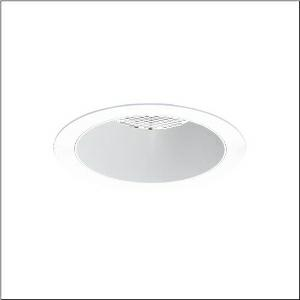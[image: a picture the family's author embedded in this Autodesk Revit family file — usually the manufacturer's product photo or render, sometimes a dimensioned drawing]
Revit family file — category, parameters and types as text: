
# Revit family: lunis_21_xl_51db18ef91c
name_source: partatom
category: Lighting Fixtures
units: mm (PartAtom-declared; Revit-internal decimal feet)

## family parameters
Cut with Voids When Loaded = No
Host = Face
Light Source = No
Part Type = Normal
Room Calculation Point = No
Round Connector Dimension = Use Diameter
Shared = No

## types (1)
- --- (1 x LED, 4070 lm, 25.4 W, 6500K)
    Apparent Load = 25 VA
    CIE Flux Codes = 87 97 99 100 100
    Color Rendering = 80
    Color Temperature = 6500K
    Default Elevation = 1800 mm
    Description = Lunis 21,  XL, downlight, light control with lens, of PMMA, anti glare with reflector, of PC, light emission: direct distribution, LED rated luminous flux: 2.410lm, light colour: 830/840/865, with terminal, 5-pole, mains connection: 220..240V, AC/DC, 0/50..60Hz, housing, round, of diecast aluminium, traffic white (RAL 9016), diameter: 230mm, clamping range: 1..40mm, protection rating (complete): IP20, protection rating (on room side): IP54, insulation class (complete): insulation class II (safety insulation), certification: CE, impact resistance: IK03, packaging unit: 1 piece
    Height = 0 mm  [stored 0 ft]
    Lamp = 1 x LED
    Lamp Light Flux = 4070 lm
    Lamp Power = 25.4 W
    Lamp count = 1
    Length = 230 mm
    Luminous efficacy = 160 lm/W
    Manufacturer = Siteco
    ModVariant = No
    Model = 51DB18EF91C
    Mounting Place = Ceiling
    Mounting Type = Recessed
    Number of Poles = 1
    OnlyDefault = Yes
    Power Factor = 1
    Product Name = Lunis 21 XL
    Product group = downlight
    ProductGroupID = 400
    Protection Class = Protection class II
    Protection Degree = IP 20
    RLX_Detail_Level = 1
    RLX_Emergency_Light_Flux = 0 lm
    RLX_Emergency_Type = 0
    RLX_Emergency_Type_DB = No
    RlxData = <blob elided: 20453 chars, md5=cce98392>
    Socket = socket
    Standby Power = 0 W
    System Light Flux = 4070 lm
    System Power = 25 W
    Type Comments = individual setting: colour temperature 6500K, luminous flux: 100 % | (ON | ON | OFF | OFF) | 700 mA
    Type Image = l_1291159.jpg
    URL = http://relux.com
    VarID = @adj_019234
    Voltage = 0 V
    Weight = 0.00 kg
    Width = 0 mm  [stored 0 ft]

note: [stored X ft] marks values corroborated as IEEE doubles in the binary element streams (Revit-internal decimal feet)

## geometry (parser evidence)
native form markers: Blend x4, Sweep x10
no freeform markers — native parametric forms only
